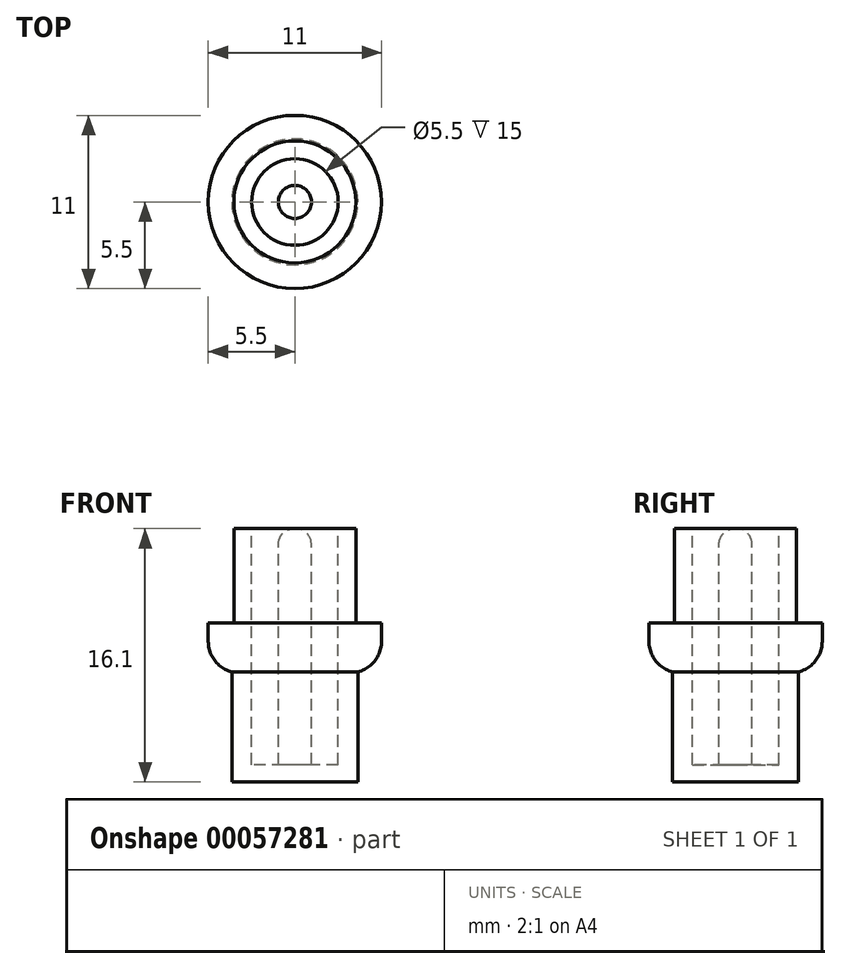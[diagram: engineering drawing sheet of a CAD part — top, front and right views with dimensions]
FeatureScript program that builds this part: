
annotation { "Feature Type Name" : "Feature", "Feature Type Description" : "" }
export const myFeature = defineFeature(function(context is Context, id is Id, definition is map)
    precondition{}
    {
        {
            var Q0;
            Q0=qCreatedBy(makeId("Top.planeOp"),FACE);
            var sketch = newSketch(context, id + "F0", { "sketchPlane" : qUnion([Q0])});
            skCircle(sketch, "E0", {"center": v(0, 0) * mm, "radius": 5.5 * mm});
            skSolve(sketch);
        }
        {
            var Q0;
            Q0 = qSketchRegion(id + "F0", true);
            extrude(context, id + "F1", {"entities" : qUnion([Q0]), "depth" : .1 * mm});
        }
        {
            var Q0;
            Q0=makeQuery(id+"F1.opExtrude","CAP_FACE",FACE,{"disambiguationData":[OSD([sQuery(id+"F0.wireOp",EDGE,"E0")])],"isStart":false});
            var sketch = newSketch(context, id + "F2", { "sketchPlane" : qUnion([Q0])});
            skCircle(sketch, "E1", {"center": v(0, 0) * mm, "radius": 3.88 * mm});
            skSolve(sketch);
        }
        {
            var Q0;
            Q0 = qSketchRegion(id + "F2", true);
            extrude(context, id + "F3", {"entities" : qUnion([Q0]), "operationType" : NewBodyOperationType.ADD, "depth" : 6 * mm});
        }
        {
            var Q0;
            Q0 = qSketchRegion(id + "F0", true);
            extrude(context, id + "F4", {"entities" : qUnion([Q0]), "operationType" : NewBodyOperationType.ADD, "oppositeDirection" : true, "depth" : 3 * mm});
        }
        {
            var Q0;
            Q0=makeQuery(id+"F4.opExtrude","CAP_FACE",FACE,{"disambiguationData":[OSD([sQuery(id+"F0.wireOp",EDGE,"E0")])],"isStart":false});
            var sketch = newSketch(context, id + "F5", { "sketchPlane" : qUnion([Q0])});
            skCircle(sketch, "E2", {"center": v(0, 0) * mm, "radius": 4 * mm});
            skSolve(sketch);
        }
        {
            var Q0;
            Q0 = qSketchRegion(id + "F5", true);
            extrude(context, id + "F6", {"entities" : qUnion([Q0]), "operationType" : NewBodyOperationType.ADD, "depth" : 7 * mm});
        }
        {
            var Q0;
            Q0=makeQuery(id+"F3.opExtrude","CAP_FACE",FACE,{"disambiguationData":[OSD([sQuery(id+"F2.wireOp",EDGE,"E1")])],"isStart":false});
            var sketch = newSketch(context, id + "F7", { "sketchPlane" : qUnion([Q0])});
            skCircle(sketch, "E3", {"center": v(0, 0) * mm, "radius": 2.75 * mm});
            skCircle(sketch, "E4", {"center": v(0, 0) * mm, "radius": 1.05 * mm});
            skSolve(sketch);
        }
        {
            var Q0;
            Q0 = qSketchRegion(id + "F7", true);
            extrude(context, id + "F8", {"entities" : qUnion([Q0]), "operationType" : NewBodyOperationType.REMOVE, "oppositeDirection" : true, "depth" : 15 * mm});
        }
        {
            var Q0;
            Q0=makeQuery(id+"F8.boolean.opBoolean","COPY",EDGE,{"derivedFrom":makeQuery(id+"F8.opExtrude","CAP_EDGE",EDGE,{"disambiguationData":[OSD([sQuery(id+"F7.wireOp",EDGE,"E4")])],"isStart":true})});
            fillet(context, id + "F9", {"entities" : qUnion([Q0]), "radius" : 1 * mm, "tangentPropagation" : true, "allowEdgeOverflow" : false});
        }
        {
            var Q0;
            Q0=makeQuery(id+"F4.opExtrude","CAP_EDGE",EDGE,{"disambiguationData":[OSD([sQuery(id+"F0.wireOp",EDGE,"E0")])],"isStart":false});
            fillet(context, id + "F10", {"entities" : qUnion([Q0]), "radius" : 2 * mm, "tangentPropagation" : true, "allowEdgeOverflow" : false});
        }
    });
